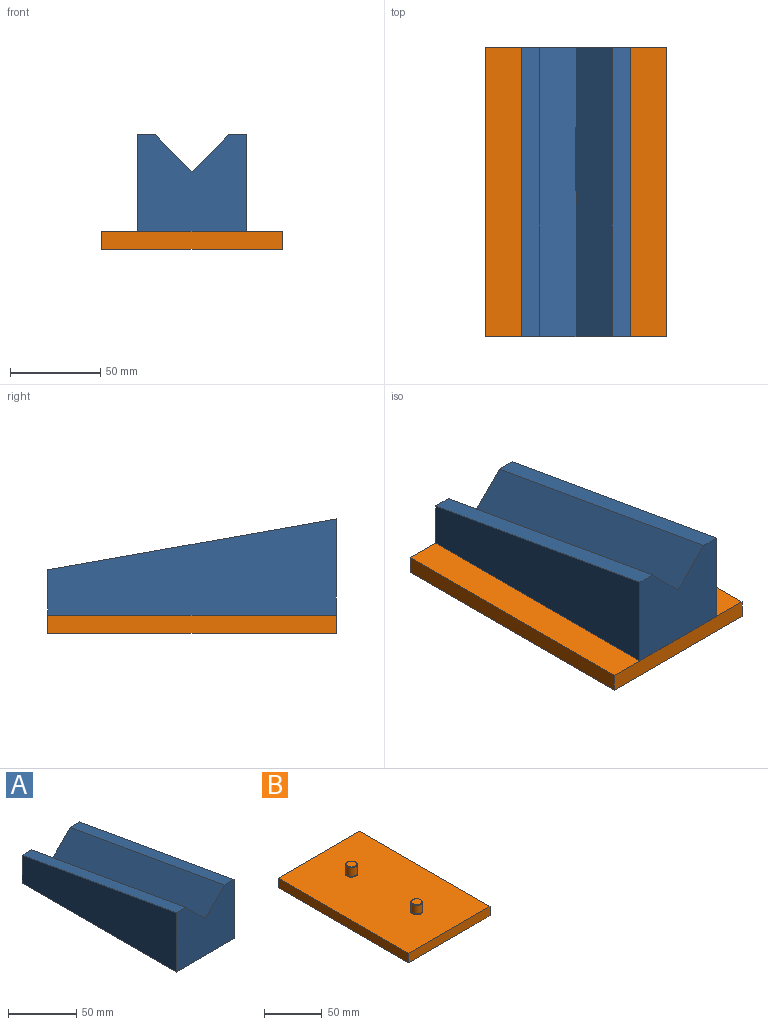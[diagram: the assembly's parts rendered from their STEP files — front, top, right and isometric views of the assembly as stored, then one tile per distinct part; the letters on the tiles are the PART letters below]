
ASSEMBLY  parts=2 mates=1
PART A: 17 faces, bbox 60x160x53.2 mm
  f0: plane 160x28.21mm, normal (0,0.17,0.98), area 1624.7mm2, adj f1,f2,f6,f8
  f1: plane 60x53.21mm, normal (0,-1,0), area 2786.6mm2, adj f0,f3,f4,f5,f6,f7,f8
  f2: plane 60x25mm, normal (0,1,0), area 1093.8mm2, adj f0,f3,f4,f5,f6,f7,f8
  f3: plane 160x60mm, normal (0,0,-1), area 9409.9mm2, adj f1,f2,f5,f6,f12,f16
  f4: plane 160x28.21mm, normal (0,0.17,0.98), area 1624.7mm2, adj f1,f2,f5,f7
  f5: plane 160x53.21mm, normal (1,0,0), area 6257mm2, adj f1,f2,f3,f4
  f6: plane 160x53.21mm, normal (-1,0,0), area 6257mm2, adj f0,f1,f2,f3
  f7: plane 160x48.52mm, normal (-0.71,0.12,0.7), area 4595.3mm2, adj f1,f2,f4,f8
  f8: plane 160x48.52mm, normal (0.71,0.12,0.7), area 4595.3mm2, adj f0,f1,f2,f7
  f9: cylinder r=5mm len=10mm, axis (0,0,-1), area 282.7mm2, adj f11,f12
  f10: plane 9x9mm, normal (0,0,-1), area 63.6mm2, adj f11
  f11: cone r=4.5mm half-angle=45deg, axis (0,0,-1), area 21.1mm2, adj f9,f10
  f12: cone r=5mm half-angle=45deg, axis (0,0,-1), area 23.3mm2, adj f3,f9
  f13: cylinder r=5mm len=10mm, axis (0,0,-1), area 282.7mm2, adj f15,f16
  f14: plane 9x9mm, normal (0,0,-1), area 63.6mm2, adj f15
  f15: cone r=5mm half-angle=45deg, axis (0,0,-1), area 21.1mm2, adj f13,f14
  f16: cone r=5.5mm half-angle=45deg, axis (0,0,-1), area 23.3mm2, adj f3,f13
PART B: 14 faces, bbox 100x160x20 mm
  f0: plane 160x100mm, normal (0,0,1), area 15809.9mm2, adj f1,f3,f4,f5,f8,f12
  f1: plane 160x10mm, normal (-1,0,0), area 1600mm2, adj f0,f2,f4,f5
  f2: plane 160x100mm, normal (0,0,-1), area 16000mm2, adj f1,f3,f4,f5
  f3: plane 160x10mm, normal (1,0,0), area 1600mm2, adj f0,f2,f4,f5
  f4: plane 100x10mm, normal (0,-1,0), area 1000mm2, adj f0,f1,f2,f3
  f5: plane 100x10mm, normal (0,1,0), area 1000mm2, adj f0,f1,f2,f3
  f6: cylinder r=5mm len=10mm, axis (0,0,-1), area 282.7mm2, adj f8,f9
  f7: plane 9x9mm, normal (0,0,1), area 63.6mm2, adj f9
  f8: cone r=5mm half-angle=45deg, axis (0,0,-1), area 23.3mm2, adj f0,f6
  f9: cone r=4.5mm half-angle=45deg, axis (0,0,-1), area 21.1mm2, adj f6,f7
  f10: cylinder r=5mm len=10mm, axis (0,0,-1), area 282.7mm2, adj f12,f13
  f11: plane 9x9mm, normal (0,0,1), area 63.6mm2, adj f13
  f12: cone r=5mm half-angle=45deg, axis (0,0,-1), area 23.3mm2, adj f0,f10
  f13: cone r=5mm half-angle=45deg, axis (0,0,-1), area 21.1mm2, adj f10,f11
PLACE A at identity
PLACE B at identity fixed
MATE slider A.f9 <-> B.f10  axis (0,0,-1) through (0,40,10)mm
